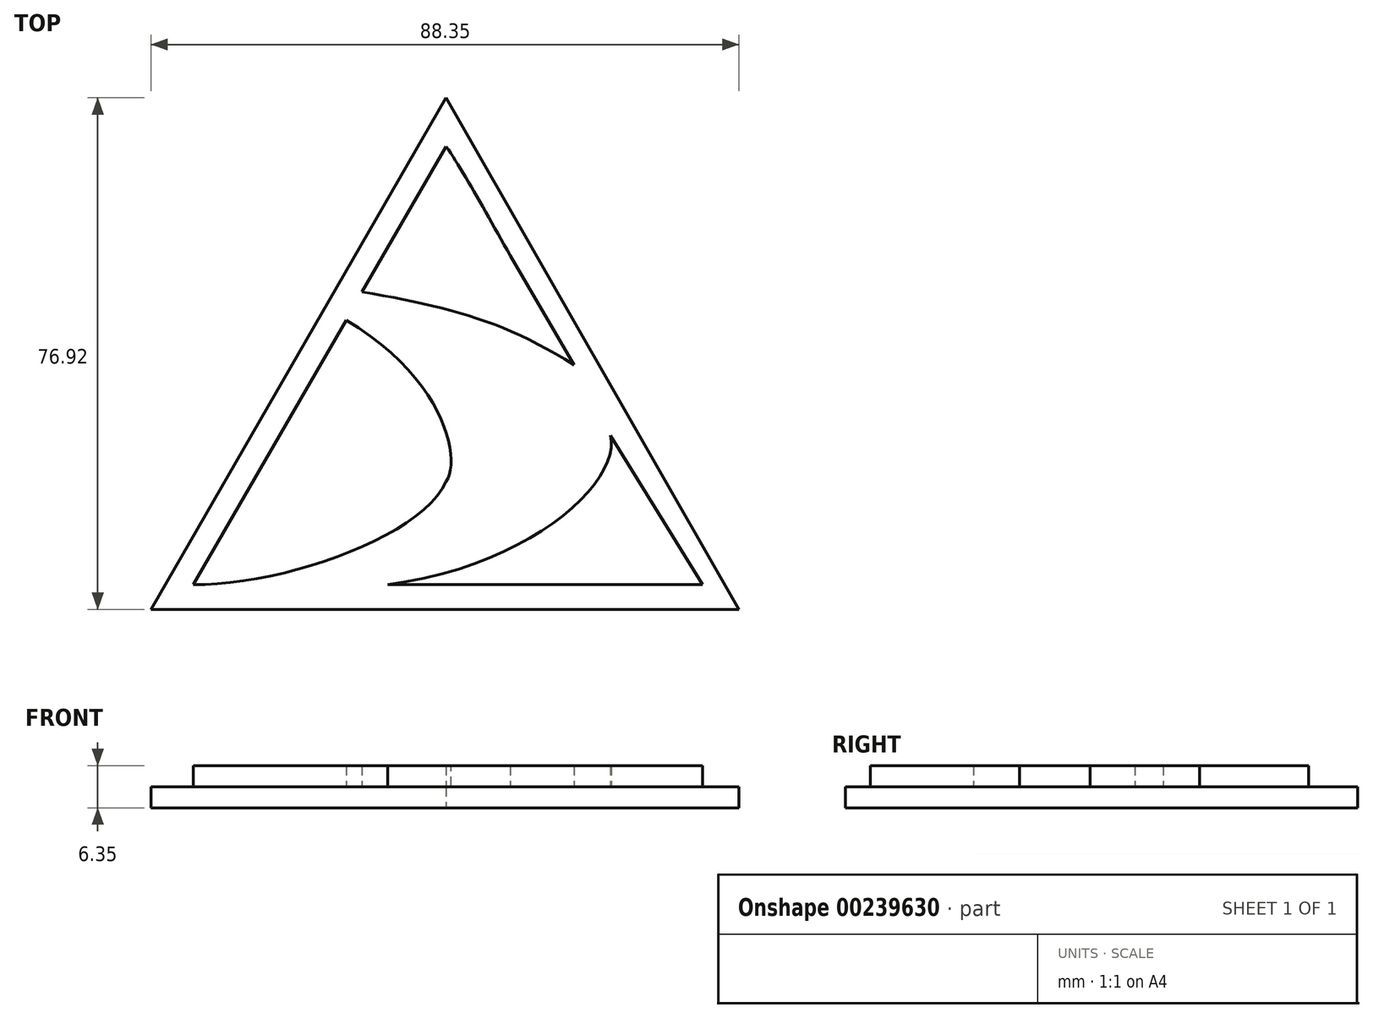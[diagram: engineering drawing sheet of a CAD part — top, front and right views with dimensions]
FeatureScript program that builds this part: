
annotation { "Feature Type Name" : "Feature", "Feature Type Description" : "" }
export const myFeature = defineFeature(function(context is Context, id is Id, definition is map)
    precondition{}
    {
        {
            var Q0;
            Q0=qCreatedBy(makeId("Top.planeOp"),FACE);
            var sketch = newSketch(context, id + "F0", { "sketchPlane" : qUnion([Q0])});
            skLineSegment(sketch, "E0", {"start": v(-12.7, 44) * mm, "end": v(0, 65.87) * mm});
            skLineSegment(sketch, "E1", {"start": v(0, 65.87) * mm, "end": v(19.23, 33.03) * mm});
            skFitSpline(sketch, "E2", {"points": [v(0, 65.87) * mm, v(19.23, 33.03) * mm], "startDerivative": vector(14.8, -21.49) * mm, "endDerivative": vector(14.8, -21.49) * mm});
            skFitSpline(sketch, "E3", {"points": [v(-12.7, 44) * mm, v(19.23, 33.03) * mm], "startDerivative": vector(38.08, -6.59) * mm, "endDerivative": vector(32.43, -20.26) * mm});
            skSolve(sketch);
        }
        {
            var Q0;
            Q0=qCreatedBy(makeId("Top.planeOp"),FACE);
            var sketch = newSketch(context, id + "F1", { "sketchPlane" : qUnion([Q0])});
            skLineSegment(sketch, "E4", {"start": v(-37.98, 0) * mm, "end": v(-15.05, 39.77) * mm});
            skFitSpline(sketch, "E5", {"points": [v(-15.05, 39.77) * mm, v(0, 15.5) * mm], "startDerivative": vector(45.14, -27.26) * mm, "endDerivative": vector(-6.58, -10.13) * mm});
            skFitSpline(sketch, "E6", {"points": [v(-37.98, 0) * mm, v(0, 15.5) * mm], "startDerivative": vector(39.71, -0.54) * mm, "endDerivative": vector(11.07, 25.13) * mm});
            skSolve(sketch);
        }
        {
            var Q0;
            Q0=qCreatedBy(makeId("Top.planeOp"),FACE);
            var sketch = newSketch(context, id + "F2", { "sketchPlane" : qUnion([Q0])});
            skLineSegment(sketch, "E7", {"start": v(24.64, 22.4) * mm, "end": v(38.5, 0) * mm});
            skLineSegment(sketch, "E8", {"start": v(38.5, 0) * mm, "end": v(-8.8, 0) * mm});
            skFitSpline(sketch, "E9", {"points": [v(24.64, 22.4) * mm, v(-8.8, 0) * mm], "startDerivative": vector(5.58, -19.75) * mm, "endDerivative": vector(-65.36, -8.43) * mm});
            skSolve(sketch);
        }
        {
            var Q0;
            Q0=qCreatedBy(makeId("Top.planeOp"),FACE);
            var sketch = newSketch(context, id + "F3", { "sketchPlane" : qUnion([Q0])});
            skLineSegment(sketch, "E10", {"start": v(0, 73.2) * mm, "end": v(-44.36, -3.73) * mm});
            skLineSegment(sketch, "E11", {"start": v(-44.36, -3.73) * mm, "end": v(43.99, -3.73) * mm});
            skLineSegment(sketch, "E12", {"start": v(43.99, -3.73) * mm, "end": v(0, 73.2) * mm});
            skSolve(sketch);
        }
        {
            var Q0;
            Q0 = qSketchRegion(id + "F0", true);
            extrude(context, id + "F4", {"entities" : qUnion([Q0]), "depth" : 6.35 * mm});
        }
        {
            var Q0;
            Q0=makeQuery(id+"F3.imprint","IMPRINT",FACE,{"disambiguationData":[TD([[makeQuery(id+"F3.imprint","IMPRINT",EDGE,{"derivedFrom":sQuery(id+"F3.wireOp",EDGE,"E10")}),1.0]])]});
            extrude(context, id + "F5", {"entities" : qUnion([Q0]), "operationType" : NewBodyOperationType.ADD, "depth" : 3.17 * mm});
        }
        {
            var Q0;
            Q0 = qSketchRegion(id + "F2", true);
            extrude(context, id + "F6", {"entities" : qUnion([Q0]), "operationType" : NewBodyOperationType.ADD, "depth" : 6.35 * mm});
        }
        {
            var Q0;
            Q0 = qSketchRegion(id + "F1", true);
            extrude(context, id + "F7", {"entities" : qUnion([Q0]), "operationType" : NewBodyOperationType.ADD, "depth" : 6.35 * mm});
        }
    });
